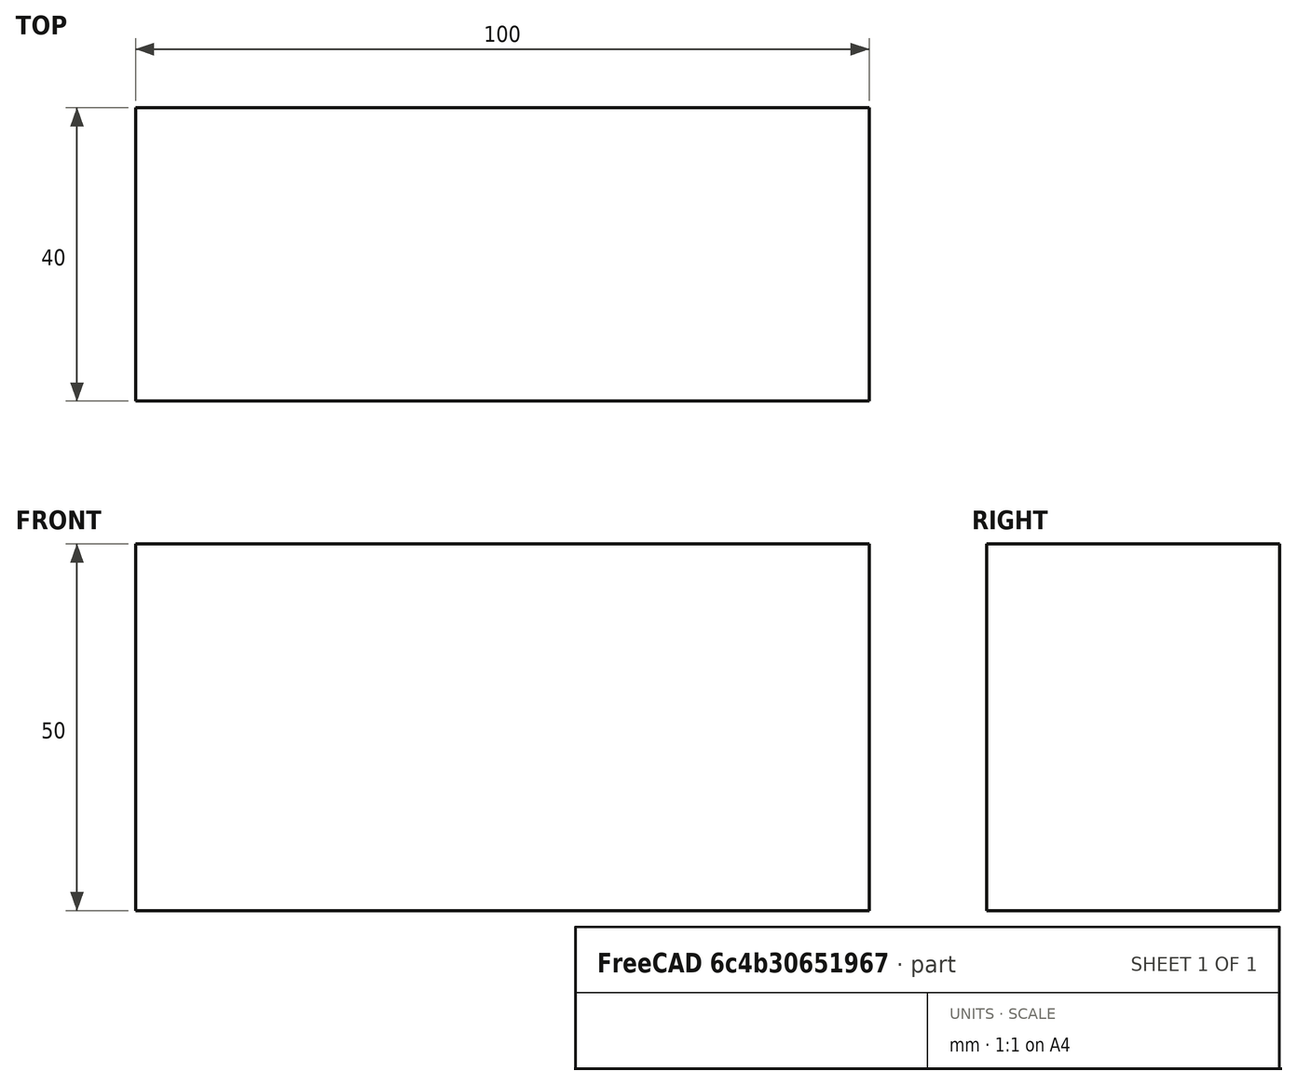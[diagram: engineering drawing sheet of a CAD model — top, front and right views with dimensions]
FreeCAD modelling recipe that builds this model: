
FCSTD DOCUMENT  (FreeCAD 0.15R4671 (Git))
Label: Flat Bar 100x40 EN10058 S235JR
License: All rights reserved
LicenseURL: http://en.wikipedia.org/wiki/All_rights_reserved
objects: Sketcher::SketchObject×1, Part::Extrusion×1
note: 2 computed .brp shape members not serialized (recipe doc carries the construction recipe); baked Part::Feature solids carry a one-line shape summary decoded from their .brp

FEATURE [Sketcher::SketchObject] Sketch
  sketch-geometry (4):
    g0: LineSegment StartX=-50 StartY=-20 StartZ=0 EndX=50 EndY=-20 EndZ=0
    g1: LineSegment StartX=50 StartY=-20 StartZ=0 EndX=50 EndY=20 EndZ=0
    g2: LineSegment StartX=50 StartY=20 StartZ=0 EndX=-50 EndY=20 EndZ=0
    g3: LineSegment StartX=-50 StartY=20 StartZ=0 EndX=-50 EndY=-20 EndZ=0
  constraints (12):
    c: Coincident(g0,g1)
    c: Coincident(g1,g2)
    c: Coincident(g2,g3)
    c: Coincident(g3,g0)
    c: Horizontal(g0)
    c: Horizontal(g2)
    c: Vertical(g1)
    c: Vertical(g3)
    c: Symmetric(g1,g2,g-2)
    c: Symmetric(g0,g1,g-1)
    c: DistanceY(g1) = 40
    c: DistanceX(g0) = 100
FEATURE [Part::Extrusion] Extrude  label="Flat Bar 100x40 EN10058 S235JR"
  Base = -> Sketch
  Dir = (0,0,50)
  Solid = true
